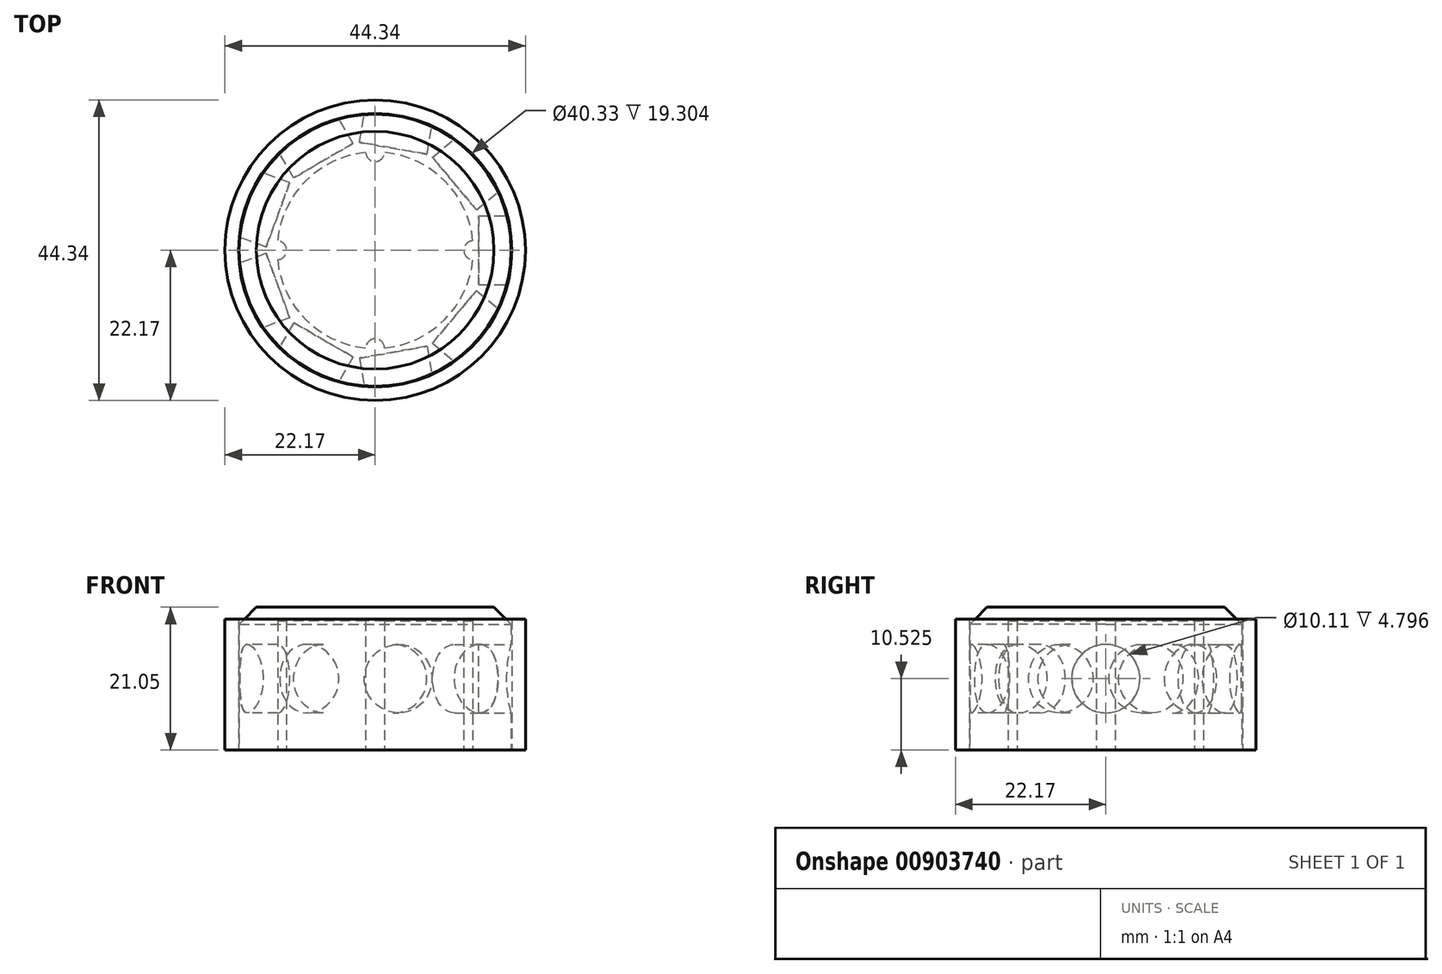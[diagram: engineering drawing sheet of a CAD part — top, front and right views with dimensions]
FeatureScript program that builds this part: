
annotation { "Feature Type Name" : "Feature", "Feature Type Description" : "" }
export const myFeature = defineFeature(function(context is Context, id is Id, definition is map)
    precondition{}
    {
        {
            var Q0;
            Q0=qCreatedBy(makeId("Front.planeOp"),FACE);
            var sketch = newSketch(context, id + "F0", { "sketchPlane" : qUnion([Q0])});
            skLineSegment(sketch, "E0", {"start": v(0, 0) * mm, "end": v(20.06, 0) * mm, "construction": true});
            skLineSegment(sketch, "E1", {"start": v(0, 19.05) * mm, "end": v(14.48, 19.05) * mm});
            skLineSegment(sketch, "E2", {"start": v(14.48, 19.05) * mm, "end": v(14.48, 0) * mm});
            skLineSegment(sketch, "E3", {"start": v(20.07, 0) * mm, "end": v(20.07, 21.05) * mm});
            skLineSegment(sketch, "E4", {"start": v(14.48, 0) * mm, "end": v(20.07, 0) * mm});
            skLineSegment(sketch, "E5", {"start": v(20.07, 21.05) * mm, "end": v(0, 21.05) * mm});
            skLineSegment(sketch, "E6", {"start": v(0, 21.05) * mm, "end": v(0, 19.05) * mm});
            skLineSegment(sketch, "E7", {"start": v(0, 0) * mm, "end": v(0, 11.66) * mm, "construction": true});
            skSolve(sketch);
        }
        {
            var Q0;
            Q0=makeQuery(id+"F0.imprint","IMPRINT",FACE,{"disambiguationData":[TD([[makeQuery(id+"F0.imprint","IMPRINT",EDGE,{"derivedFrom":sQuery(id+"F0.wireOp",EDGE,"E1")}),1.0]])]});
            var Q1;
            Q1=sQuery(id+"F0.wireOp",EDGE,"E7");
            revolve(context, id + "F1", {"surfaceOperationType" : NewSurfaceOperationType.NEW, "entities" : qUnion([Q0]), "axis" : qUnion([Q1]), "revolveType" : RevolveType.FULL});
        }
        {
            var Q0;
            Q0=makeQuery(id+"F1.opRevolve","SWEPT_FACE",FACE,{"disambiguationData":[OSD([sQuery(id+"F0.wireOp",EDGE,"E4")])]});
            var sketch = newSketch(context, id + "F2", { "sketchPlane" : qUnion([Q0])});
            skCircle(sketch, "E8.0.0", {"center": v(0, 0) * mm, "radius": 20.07 * mm});
            skCircle(sketch, "E9.0", {"center": v(0, 0) * mm, "radius": 14.48 * mm});
            skPoint(sketch, "E10", {"position": v(0, 14.48) * mm});
            skCircle(sketch, "E11", {"center": v(0, 14.48) * mm, "radius": 1.4 * mm});
            skCircle(sketch, "E12.1.0", {"center": v(14.48, 0) * mm, "radius": 1.4 * mm});
            skCircle(sketch, "E12.2.0", {"center": v(0, -14.48) * mm, "radius": 1.4 * mm});
            skCircle(sketch, "E12.3.0", {"center": v(-14.48, 0) * mm, "radius": 1.4 * mm});
            skLineSegment(sketch, "E12.anchor1", {"start": v(0, 0) * mm, "end": v(0, 14.48) * mm, "construction": true});
            skLineSegment(sketch, "E12.anchor2", {"start": v(0, 0) * mm, "end": v(-14.48, 0) * mm, "construction": true});
            skSolve(sketch);
        }
        {
            var Q0;
            {var subQ0=sQuery(id+"F2.wireOp",EDGE,"E12.4.0");var subQ1=sQuery(id+"F2.wireOp",EDGE,"E9.0");var subQ2=makeQuery(id+"F2.imprint","INTERSECT",VERTEX,{"disambiguationData":[OD(0.0)],"derivedFrom":[subQ1,subQ0]});Q0=makeQuery(id+"F2.imprint","IMPRINT",FACE,{"disambiguationData":[TD([[makeQuery(id+"F2.imprint","IMPRINT",EDGE,{"disambiguationData":[TD([[subQ2,-1.0]])],"derivedFrom":subQ1}),1.0]])]});}
            var Q1;
            {var subQ0=sQuery(id+"F2.wireOp",EDGE,"E12.4.0");var subQ1=sQuery(id+"F2.wireOp",EDGE,"E9.0");var subQ2=makeQuery(id+"F2.imprint","INTERSECT",VERTEX,{"disambiguationData":[OD(0.0)],"derivedFrom":[subQ1,subQ0]});Q1=makeQuery(id+"F2.imprint","IMPRINT",FACE,{"disambiguationData":[TD([[makeQuery(id+"F2.imprint","IMPRINT",EDGE,{"disambiguationData":[TD([[subQ2,-1.0]])],"derivedFrom":subQ1}),-1.0]])]});}
            var Q2;
            {var subQ0=sQuery(id+"F2.wireOp",EDGE,"E11");var subQ1=sQuery(id+"F2.wireOp",EDGE,"E9.0");var subQ2=makeQuery(id+"F2.imprint","INTERSECT",VERTEX,{"disambiguationData":[OD(0.0)],"derivedFrom":[subQ1,subQ0]});Q2=makeQuery(id+"F2.imprint","IMPRINT",FACE,{"disambiguationData":[TD([[makeQuery(id+"F2.imprint","IMPRINT",EDGE,{"disambiguationData":[TD([[subQ2,-1.0]])],"derivedFrom":subQ1}),-1.0]])]});}
            var Q3;
            {var subQ0=sQuery(id+"F2.wireOp",EDGE,"E11");var subQ1=sQuery(id+"F2.wireOp",EDGE,"E9.0");var subQ2=makeQuery(id+"F2.imprint","INTERSECT",VERTEX,{"disambiguationData":[OD(0.0)],"derivedFrom":[subQ1,subQ0]});Q3=makeQuery(id+"F2.imprint","IMPRINT",FACE,{"disambiguationData":[TD([[makeQuery(id+"F2.imprint","IMPRINT",EDGE,{"disambiguationData":[TD([[subQ2,-1.0]])],"derivedFrom":subQ1}),1.0]])]});}
            var Q4;
            {var subQ0=sQuery(id+"F2.wireOp",EDGE,"E12.1.0");var subQ1=sQuery(id+"F2.wireOp",EDGE,"E9.0");var subQ2=makeQuery(id+"F2.imprint","INTERSECT",VERTEX,{"disambiguationData":[OD(0.0)],"derivedFrom":[subQ1,subQ0]});Q4=makeQuery(id+"F2.imprint","IMPRINT",FACE,{"disambiguationData":[TD([[makeQuery(id+"F2.imprint","IMPRINT",EDGE,{"disambiguationData":[TD([[subQ2,-1.0]])],"derivedFrom":subQ1}),1.0]])]});}
            var Q5;
            {var subQ0=sQuery(id+"F2.wireOp",EDGE,"E12.1.0");var subQ1=sQuery(id+"F2.wireOp",EDGE,"E9.0");var subQ2=makeQuery(id+"F2.imprint","INTERSECT",VERTEX,{"disambiguationData":[OD(0.0)],"derivedFrom":[subQ1,subQ0]});Q5=makeQuery(id+"F2.imprint","IMPRINT",FACE,{"disambiguationData":[TD([[makeQuery(id+"F2.imprint","IMPRINT",EDGE,{"disambiguationData":[TD([[subQ2,-1.0]])],"derivedFrom":subQ1}),-1.0]])]});}
            var Q6;
            {var subQ0=sQuery(id+"F2.wireOp",EDGE,"E12.2.0");var subQ1=sQuery(id+"F2.wireOp",EDGE,"E9.0");var subQ2=makeQuery(id+"F2.imprint","INTERSECT",VERTEX,{"disambiguationData":[OD(0.0)],"derivedFrom":[subQ1,subQ0]});Q6=makeQuery(id+"F2.imprint","IMPRINT",FACE,{"disambiguationData":[TD([[makeQuery(id+"F2.imprint","IMPRINT",EDGE,{"disambiguationData":[TD([[subQ2,-1.0]])],"derivedFrom":subQ1}),1.0]])]});}
            var Q7;
            {var subQ0=sQuery(id+"F2.wireOp",EDGE,"E12.2.0");var subQ1=sQuery(id+"F2.wireOp",EDGE,"E9.0");var subQ2=makeQuery(id+"F2.imprint","INTERSECT",VERTEX,{"disambiguationData":[OD(0.0)],"derivedFrom":[subQ1,subQ0]});Q7=makeQuery(id+"F2.imprint","IMPRINT",FACE,{"disambiguationData":[TD([[makeQuery(id+"F2.imprint","IMPRINT",EDGE,{"disambiguationData":[TD([[subQ2,-1.0]])],"derivedFrom":subQ1}),-1.0]])]});}
            var Q8;
            {var subQ0=sQuery(id+"F2.wireOp",EDGE,"E12.3.0");var subQ1=sQuery(id+"F2.wireOp",EDGE,"E9.0");var subQ2=makeQuery(id+"F2.imprint","INTERSECT",VERTEX,{"disambiguationData":[OD(0.0)],"derivedFrom":[subQ1,subQ0]});Q8=makeQuery(id+"F2.imprint","IMPRINT",FACE,{"disambiguationData":[TD([[makeQuery(id+"F2.imprint","IMPRINT",EDGE,{"disambiguationData":[TD([[subQ2,1.0]])],"derivedFrom":subQ1}),-1.0]])]});}
            var Q9;
            {var subQ0=sQuery(id+"F2.wireOp",EDGE,"E12.3.0");var subQ1=sQuery(id+"F2.wireOp",EDGE,"E9.0");var subQ2=makeQuery(id+"F2.imprint","INTERSECT",VERTEX,{"disambiguationData":[OD(0.0)],"derivedFrom":[subQ1,subQ0]});Q9=makeQuery(id+"F2.imprint","IMPRINT",FACE,{"disambiguationData":[TD([[makeQuery(id+"F2.imprint","IMPRINT",EDGE,{"disambiguationData":[TD([[subQ2,1.0]])],"derivedFrom":subQ1}),1.0]])]});}
            var Q10;
            Q10=makeQuery(id+"F1.opRevolve","SWEPT_FACE",FACE,{"disambiguationData":[OSD([sQuery(id+"F0.wireOp",EDGE,"E1")])]});
            extrude(context, id + "F3", {"entities" : qUnion([Q0, Q1, Q2, Q3, Q4, Q5, Q6, Q7, Q8, Q9]), "operationType" : NewBodyOperationType.ADD, "endBound" : BoundingType.UP_TO_SURFACE, "oppositeDirection" : true, "depth" : 25.4 * mm, "endBoundEntityFace" : qUnion([Q10]), "offsetDistance" : 25.4 * mm});
        }
        {
            var Q0;
            Q0=qCreatedBy(makeId("Right.planeOp"),FACE);
            cPlane(context, id + "F4", {"entities" : qUnion([Q0]), "cplaneType" : CPlaneType.OFFSET, "offset" : 40.13 * mm / 2, "width" : 152.4 * mm, "height" : 152.4 * mm});
        }
        {
            var Q0;
            Q0=qCreatedBy(id+"F4.planeOp",FACE);
            var sketch = newSketch(context, id + "F5", { "sketchPlane" : qUnion([Q0])});
            skLineSegment(sketch, "E13", {"start": v(-20.07, 0) * mm, "end": v(-20.07, 21.05) * mm});
            skLineSegment(sketch, "E14", {"start": v(20.07, 21.05) * mm, "end": v(20.07, 0) * mm});
            skLineSegment(sketch, "E15", {"start": v(-20.07, 10.53) * mm, "end": v(20.07, 10.53) * mm, "construction": true});
            skLineSegment(sketch, "E16.0", {"start": v(20.07, 21.05) * mm, "end": v(-20.07, 21.05) * mm});
            skLineSegment(sketch, "E17", {"start": v(0, 0) * mm, "end": v(0, 21.05) * mm, "construction": true});
            skPoint(sketch, "E18", {"position": v(0, 10.53) * mm});
            skCircle(sketch, "E19", {"center": v(0, 10.53) * mm, "radius": 5.05 * mm});
            skSolve(sketch);
        }
        {
            var Q0;
            Q0=makeQuery(id+"F5.imprint","IMPRINT",FACE,{"disambiguationData":[TD([[makeQuery(id+"F5.imprint","IMPRINT",EDGE,{"derivedFrom":sQuery(id+"F5.wireOp",EDGE,"E19")}),1.0]])]});
            extrude(context, id + "F6", {"entities" : qUnion([Q0]), "oppositeDirection" : true, "depth" : 4.8 * mm, "offsetDistance" : 25.4 * mm});
        }
        {
            var Q0;
            Q0=makeQuery(id+"F6.opExtrude","SWEPT_BODY",BODY,{"disambiguationData":[OSD([sQuery(id+"F5.wireOp",EDGE,"E19")])]});
            var Q1;
            Q1=sQuery(id+"F0.wireOp",EDGE,"E7");
            circularPattern(context, id + "F7", {"entities" : qUnion([Q0]), "axis" : qUnion([Q1]), "angle" : 360 * degree, "instanceCount" : 9, "equalSpace" : true});
        }
        {
            var Q0;
            Q0=makeQuery(id+"F6.opExtrude","SWEPT_BODY",BODY,{"disambiguationData":[OSD([sQuery(id+"F5.wireOp",EDGE,"E19")])]});
            var Q1;
            Q1=makeQuery(id+"F7.opPattern","COPY",BODY,{"derivedFrom":makeQuery(id+"F6.opExtrude","SWEPT_BODY",BODY,{"disambiguationData":[OSD([sQuery(id+"F5.wireOp",EDGE,"E19")])]}),"instanceName":"2"});
            var Q2;
            Q2=makeQuery(id+"F7.opPattern","COPY",BODY,{"derivedFrom":makeQuery(id+"F6.opExtrude","SWEPT_BODY",BODY,{"disambiguationData":[OSD([sQuery(id+"F5.wireOp",EDGE,"E19")])]}),"instanceName":"4"});
            var Q3;
            Q3=makeQuery(id+"F7.opPattern","COPY",BODY,{"derivedFrom":makeQuery(id+"F6.opExtrude","SWEPT_BODY",BODY,{"disambiguationData":[OSD([sQuery(id+"F5.wireOp",EDGE,"E19")])]}),"instanceName":"6"});
            var Q4;
            Q4=makeQuery(id+"F7.opPattern","COPY",BODY,{"derivedFrom":makeQuery(id+"F6.opExtrude","SWEPT_BODY",BODY,{"disambiguationData":[OSD([sQuery(id+"F5.wireOp",EDGE,"E19")])]}),"instanceName":"8"});
            var Q5;
            Q5=makeQuery(id+"F7.opPattern","COPY",BODY,{"derivedFrom":makeQuery(id+"F6.opExtrude","SWEPT_BODY",BODY,{"disambiguationData":[OSD([sQuery(id+"F5.wireOp",EDGE,"E19")])]}),"instanceName":"9"});
            var Q6;
            Q6=makeQuery(id+"F7.opPattern","COPY",BODY,{"derivedFrom":makeQuery(id+"F6.opExtrude","SWEPT_BODY",BODY,{"disambiguationData":[OSD([sQuery(id+"F5.wireOp",EDGE,"E19")])]}),"instanceName":"7"});
            var Q7;
            Q7=makeQuery(id+"F7.opPattern","COPY",BODY,{"derivedFrom":makeQuery(id+"F6.opExtrude","SWEPT_BODY",BODY,{"disambiguationData":[OSD([sQuery(id+"F5.wireOp",EDGE,"E19")])]}),"instanceName":"5"});
            var Q8;
            Q8=makeQuery(id+"F7.opPattern","COPY",BODY,{"derivedFrom":makeQuery(id+"F6.opExtrude","SWEPT_BODY",BODY,{"disambiguationData":[OSD([sQuery(id+"F5.wireOp",EDGE,"E19")])]}),"instanceName":"3"});
            var Q9;
            Q9=makeQuery(id+"F7.opPattern","COPY",BODY,{"derivedFrom":makeQuery(id+"F6.opExtrude","SWEPT_BODY",BODY,{"disambiguationData":[OSD([sQuery(id+"F5.wireOp",EDGE,"E19")])]}),"instanceName":"1"});
            var Q10;
            Q10=makeQuery(id+"F1.opRevolve","SWEPT_BODY",BODY,{"disambiguationData":[OSD([sQuery(id+"F0.wireOp",EDGE,"E1"),sQuery(id+"F0.wireOp",EDGE,"E2"),sQuery(id+"F0.wireOp",EDGE,"E3"),sQuery(id+"F0.wireOp",EDGE,"E4"),sQuery(id+"F0.wireOp",EDGE,"E5"),sQuery(id+"F0.wireOp",EDGE,"E6")])]});
            booleanBodies(context, id + "F8", {"operationType" : BooleanOperationType.SUBTRACTION, "tools" : qUnion([Q0, Q1, Q2, Q3, Q4, Q5, Q6, Q7, Q8, Q9]), "targets" : qUnion([Q10])});
        }
        {
            var Q0;
            Q0=makeQuery(id+"F1.opRevolve","SWEPT_EDGE",EDGE,{"disambiguationData":[OSD([sQuery(id+"F0.wireOp",EDGE,"E3"),sQuery(id+"F0.wireOp",EDGE,"E5")])]});
            chamfer(context, id + "F9", {"entities" : qUnion([Q0]), "width" : 2.54 * mm, "tangentPropagation" : true});
        }
        {
            var Q0;
            Q0=makeQuery(id+"F3.boolean.opBoolean","MERGE",FACE,{"derivedFrom":[makeQuery(id+"F1.opRevolve","SWEPT_FACE",FACE,{"disambiguationData":[OSD([sQuery(id+"F0.wireOp",EDGE,"E4")])]}),makeQuery(id+"F3.opExtrude","CAP_FACE",FACE,{"disambiguationData":[OSD([sQuery(id+"F2.wireOp",EDGE,"E11")])],"isStart":true}),makeQuery(id+"F3.opExtrude","CAP_FACE",FACE,{"disambiguationData":[OSD([sQuery(id+"F2.wireOp",EDGE,"E12.1.0")])],"isStart":true}),makeQuery(id+"F3.opExtrude","CAP_FACE",FACE,{"disambiguationData":[OSD([sQuery(id+"F2.wireOp",EDGE,"E12.2.0")])],"isStart":true}),makeQuery(id+"F3.opExtrude","CAP_FACE",FACE,{"disambiguationData":[OSD([sQuery(id+"F2.wireOp",EDGE,"E12.3.0")])],"isStart":true}),makeQuery(id+"F3.opExtrude","CAP_FACE",FACE,{"disambiguationData":[OSD([sQuery(id+"F2.wireOp",EDGE,"E12.4.0")])],"isStart":true})]});
            var sketch = newSketch(context, id + "F10", { "sketchPlane" : qUnion([Q0])});
            skCircle(sketch, "E20.0", {"center": v(0, 0) * mm, "radius": 20.07 * mm});
            skCircle(sketch, "E21.0", {"center": v(0, 0) * mm, "radius": 20.17 * mm});
            skCircle(sketch, "E22.0", {"center": v(0, 0) * mm, "radius": 22.17 * mm});
            skSolve(sketch);
        }
        {
            var Q0;
            Q0=makeQuery(id+"F10.imprint","IMPRINT",FACE,{"disambiguationData":[TD([[makeQuery(id+"F10.imprint","IMPRINT",EDGE,{"derivedFrom":sQuery(id+"F10.wireOp",EDGE,"E21.0")}),-1.0]])]});
            extrude(context, id + "F11", {"entities" : qUnion([Q0]), "oppositeDirection" : true, "depth" : 19.3 * mm, "offsetDistance" : 25.4 * mm});
        }
    });
